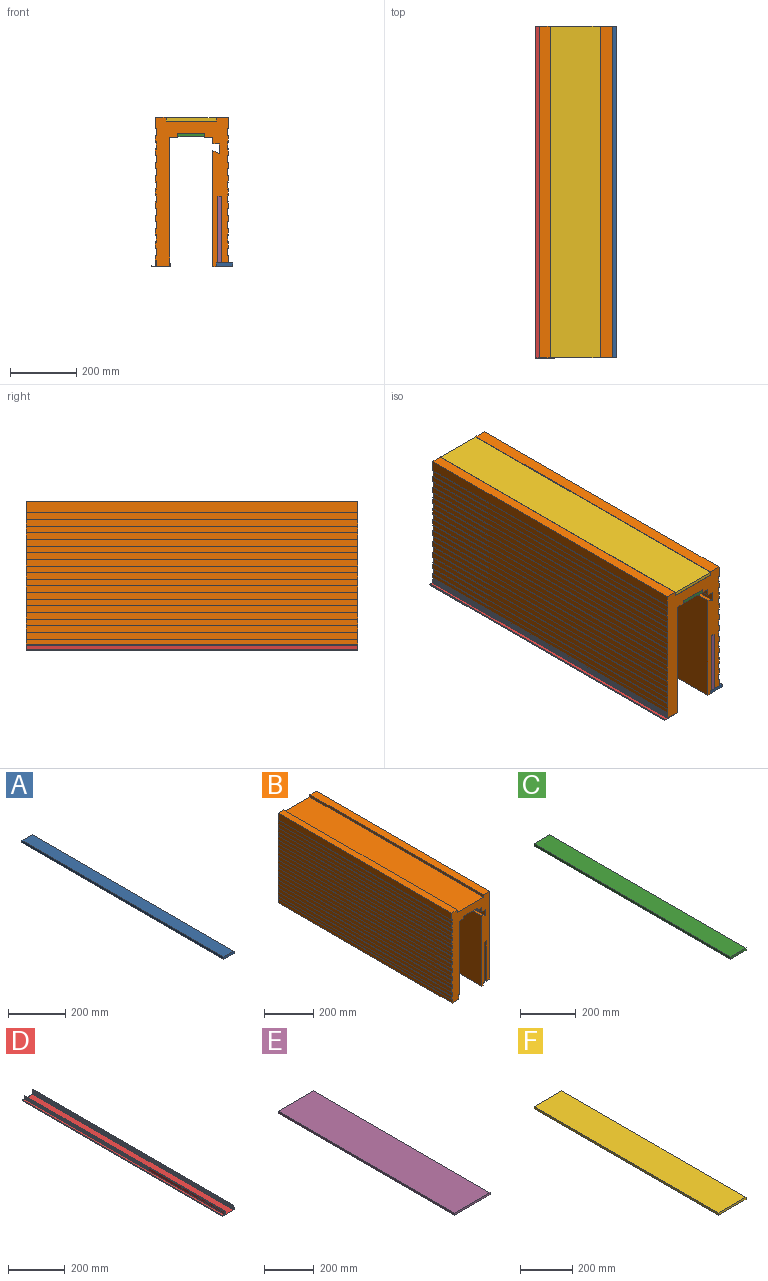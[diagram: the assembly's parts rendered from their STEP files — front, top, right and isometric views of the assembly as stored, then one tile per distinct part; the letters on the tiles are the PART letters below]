
ASSEMBLY  parts=6 mates=5
PART A: 6 faces, bbox 50x1000x10 mm
  f0: plane 1000x10mm, normal (-1,0,0), area 10000mm2, adj f1,f3,f4,f5
  f1: plane 1000x50mm, normal (0,0,-1), area 50000mm2, adj f0,f2,f4,f5
  f2: plane 1000x10mm, normal (1,0,0), area 10000mm2, adj f1,f3,f4,f5
  f3: plane 1000x50mm, normal (0,0,1), area 50000mm2, adj f0,f2,f4,f5
  f4: plane 50x10mm, normal (0,-1,0), area 500mm2, adj f0,f1,f2,f3
  f5: plane 50x10mm, normal (0,1,0), area 500mm2, adj f0,f1,f2,f3
PART B: 112 faces, bbox 220x1000x450 mm
  f0: plane 1000x35mm, normal (1,0,0), area 35000mm2, adj f1,f109,f110,f111
  f1: plane 1000x36.6mm, normal (0,0,1), area 36600mm2, adj f0,f2,f110,f111
  f2: plane 1000x11.5mm, normal (-1,0,0), area 11500mm2, adj f1,f3,f110,f111
  f3: plane 1000x151mm, normal (0,0,1), area 151000mm2, adj f2,f4,f110,f111
  f4: plane 1000x11.5mm, normal (1,0,0), area 11500mm2, adj f3,f5,f110,f111
  f5: plane 1000x32.4mm, normal (0,0,1), area 32400mm2, adj f4,f6,f110,f111
  f6: plane 1000x35mm, normal (-1,0,0), area 35000mm2, adj f5,f7,f110,f111
  f7: plane 1000x2mm, normal (0.45,0,-0.89), area 2236.1mm2, adj f6,f8,f110,f111
  f8: plane 1000x22mm, normal (-1,0,0), area 22000mm2, adj f7,f9,f110,f111
  f9: plane 1000x2mm, normal (0.45,0,0.89), area 2236.1mm2, adj f8,f10,f110,f111
  f10: plane 1000x20mm, normal (-1,0,0), area 20000mm2, adj f9,f11,f110,f111
  f11: plane 1000x2mm, normal (0.45,0,-0.89), area 2236.1mm2, adj f10,f12,f110,f111
  f12: plane 1000x22mm, normal (-1,0,0), area 22000mm2, adj f11,f13,f110,f111
  f13: plane 1000x2mm, normal (0.45,0,0.89), area 2236.1mm2, adj f12,f14,f110,f111
  f14: plane 1000x20mm, normal (-1,0,0), area 20000mm2, adj f13,f15,f110,f111
  f15: plane 1000x2mm, normal (0.45,0,-0.89), area 2236.1mm2, adj f14,f16,f110,f111
  f16: plane 1000x22mm, normal (-1,0,0), area 22000mm2, adj f15,f17,f110,f111
  f17: plane 1000x2mm, normal (0.45,0,0.89), area 2236.1mm2, adj f16,f18,f110,f111
  f18: plane 1000x20mm, normal (-1,0,0), area 20000mm2, adj f17,f19,f110,f111
  f19: plane 1000x2mm, normal (0.45,0,-0.89), area 2236.1mm2, adj f18,f20,f110,f111
  f20: plane 1000x22mm, normal (-1,0,0), area 22000mm2, adj f19,f21,f110,f111
  f21: plane 1000x2mm, normal (0.45,0,0.89), area 2236.1mm2, adj f20,f22,f110,f111
  f22: plane 1000x20mm, normal (-1,0,0), area 20000mm2, adj f21,f23,f110,f111
  f23: plane 1000x2mm, normal (0.45,0,-0.89), area 2236.1mm2, adj f22,f24,f110,f111
  f24: plane 1000x22mm, normal (-1,0,0), area 22000mm2, adj f23,f25,f110,f111
  f25: plane 1000x2mm, normal (0.45,0,0.89), area 2236.1mm2, adj f24,f26,f110,f111
  f26: plane 1000x20mm, normal (-1,0,0), area 20000mm2, adj f25,f27,f110,f111
  f27: plane 1000x2mm, normal (0.45,0,-0.89), area 2236.1mm2, adj f26,f28,f110,f111
  f28: plane 1000x22mm, normal (-1,0,0), area 22000mm2, adj f27,f29,f110,f111
  f29: plane 1000x2mm, normal (0.45,0,0.89), area 2236.1mm2, adj f28,f30,f110,f111
  f30: plane 1000x20mm, normal (-1,0,0), area 20000mm2, adj f29,f31,f110,f111
  f31: plane 1000x2mm, normal (0.45,0,-0.89), area 2236.1mm2, adj f30,f32,f110,f111
  f32: plane 1000x22mm, normal (-1,0,0), area 22000mm2, adj f31,f33,f110,f111
  f33: plane 1000x2mm, normal (0.45,0,0.89), area 2236.1mm2, adj f32,f34,f110,f111
  f34: plane 1000x20mm, normal (-1,0,0), area 20000mm2, adj f33,f35,f110,f111
  f35: plane 1000x2mm, normal (0.45,0,-0.89), area 2236.1mm2, adj f34,f36,f110,f111
  f36: plane 1000x22mm, normal (-1,0,0), area 22000mm2, adj f35,f37,f110,f111
  f37: plane 1000x2mm, normal (0.45,0,0.89), area 2236.1mm2, adj f36,f38,f110,f111
  f38: plane 1000x20mm, normal (-1,0,0), area 20000mm2, adj f37,f39,f110,f111
  f39: plane 1000x2mm, normal (0.45,0,-0.89), area 2236.1mm2, adj f38,f40,f110,f111
  f40: plane 1000x22mm, normal (-1,0,0), area 22000mm2, adj f39,f41,f110,f111
  f41: plane 1000x2mm, normal (0.45,0,0.89), area 2236.1mm2, adj f40,f42,f110,f111
  f42: plane 1000x20mm, normal (-1,0,0), area 20000mm2, adj f41,f43,f110,f111
  f43: plane 1000x2mm, normal (0.45,0,-0.89), area 2236.1mm2, adj f42,f44,f110,f111
  f44: plane 1000x22mm, normal (-1,0,0), area 22000mm2, adj f43,f45,f110,f111
  f45: plane 1000x2mm, normal (0.45,0,0.89), area 2236.1mm2, adj f44,f46,f110,f111
  f46: plane 1000x15mm, normal (-1,0,0), area 15000mm2, adj f45,f47,f110,f111
  f47: plane 1000x1.9mm, normal (0,0,-1), area 1899.3mm2, adj f46,f48,f110,f111
  f48: plane 1000x18.5mm, normal (-1,0,0), area 18504.2mm2, adj f47,f49,f110,f111
  f49: plane 1000x39.1mm, normal (0,0,-1), area 39100mm2, adj f48,f50,f110,f111
  f50: plane 1000x21.53mm, normal (1,0,0), area 21529.7mm2, adj f49,f51,f110,f111
  f51: plane 1000x1.9mm, normal (0,0,-1), area 1900.7mm2, adj f50,f52,f110,f111
  f52: plane 1000x367mm, normal (1,0,0), area 367000mm2, adj f51,f53,f110,f111
  f53: plane 1000x24.5mm, normal (0,0,-1), area 24500mm2, adj f52,f54,f110,f111
  f54: plane 1000x11.5mm, normal (1,0,0), area 11500mm2, adj f53,f55,f110,f111
  f55: plane 1000x81mm, normal (0,0,-1), area 81000mm2, adj f54,f56,f110,f111
  f56: plane 1000x11.5mm, normal (-1,0,0), area 11500mm2, adj f55,f57,f110,f111
  f57: plane 1000x24.5mm, normal (0,0,-1), area 24500mm2, adj f56,f58,f110,f111
  f58: plane 1000x20mm, normal (-1,0,0), area 20000mm2, adj f57,f59,f110,f111
  f59: plane 1000x20mm, normal (0,0,-1), area 20000mm2, adj f58,f60,f110,f111
  f60: plane 1000x30mm, normal (-1,0,0), area 30000mm2, adj f59,f61,f110,f111
  f61: plane 1000x20mm, normal (0.45,0,0.89), area 22360.7mm2, adj f60,f62,f110,f111
  f62: plane 1000x350mm, normal (-1,0,0), area 350000mm2, adj f61,f63,f110,f111
  f63: plane 1000x10.1mm, normal (0,0,-1), area 10100mm2, adj f62,f64,f110,f111
  f64: plane 1000x11.5mm, normal (1,0,0), area 11500mm2, adj f63,f65,f110,f111
  f65: plane 1000x5mm, normal (0,0,-1), area 5000mm2, adj f64,f66,f110,f111
  f66: plane 1000x201mm, normal (1,0,0), area 201000mm2, adj f65,f67,f110,f111
  f67: plane 1000x10.8mm, normal (0,0,-1), area 10800mm2, adj f66,f68,f110,f111
  f68: plane 1000x201mm, normal (-1,0,0), area 201000mm2, adj f67,f69,f110,f111
  f69: plane 1000x21.2mm, normal (0,0,-1), area 21200mm2, adj f68,f70,f110,f111
  f70: plane 1000x23.5mm, normal (1,0,0), area 23500mm2, adj f69,f71,f110,f111
  f71: plane 1000x2mm, normal (-0.45,0,0.89), area 2236.1mm2, adj f70,f72,f110,f111
  f72: plane 1000x22mm, normal (1,0,0), area 22000mm2, adj f71,f73,f110,f111
  f73: plane 1000x2mm, normal (-0.45,0,-0.89), area 2236.1mm2, adj f72,f74,f110,f111
  f74: plane 1000x20mm, normal (1,0,0), area 20000mm2, adj f73,f75,f110,f111
  f75: plane 1000x2mm, normal (-0.45,0,0.89), area 2236.1mm2, adj f74,f76,f110,f111
  f76: plane 1000x22mm, normal (1,0,0), area 22000mm2, adj f75,f77,f110,f111
  f77: plane 1000x2mm, normal (-0.45,0,-0.89), area 2236.1mm2, adj f76,f78,f110,f111
  f78: plane 1000x20mm, normal (1,0,0), area 20000mm2, adj f77,f79,f110,f111
  f79: plane 1000x2mm, normal (-0.45,0,0.89), area 2236.1mm2, adj f78,f80,f110,f111
  f80: plane 1000x22mm, normal (1,0,0), area 22000mm2, adj f79,f81,f110,f111
  f81: plane 1000x2mm, normal (-0.45,0,-0.89), area 2236.1mm2, adj f80,f82,f110,f111
  f82: plane 1000x20mm, normal (1,0,0), area 20000mm2, adj f81,f83,f110,f111
  f83: plane 1000x2mm, normal (-0.45,0,0.89), area 2236.1mm2, adj f82,f84,f110,f111
  f84: plane 1000x22mm, normal (1,0,0), area 22000mm2, adj f83,f85,f110,f111
  f85: plane 1000x2mm, normal (-0.45,0,-0.89), area 2236.1mm2, adj f84,f86,f110,f111
  f86: plane 1000x20mm, normal (1,0,0), area 20000mm2, adj f85,f87,f110,f111
  f87: plane 1000x2mm, normal (-0.45,0,0.89), area 2236.1mm2, adj f86,f88,f110,f111
  f88: plane 1000x22mm, normal (1,0,0), area 22000mm2, adj f87,f89,f110,f111
  f89: plane 1000x2mm, normal (-0.45,0,-0.89), area 2236.1mm2, adj f88,f90,f110,f111
  f90: plane 1000x20mm, normal (1,0,0), area 20000mm2, adj f89,f91,f110,f111
  f91: plane 1000x2mm, normal (-0.45,0,0.89), area 2236.1mm2, adj f90,f92,f110,f111
  f92: plane 1000x22mm, normal (1,0,0), area 22000mm2, adj f91,f93,f110,f111
  f93: plane 1000x2mm, normal (-0.45,0,-0.89), area 2236.1mm2, adj f92,f94,f110,f111
  f94: plane 1000x20mm, normal (1,0,0), area 20000mm2, adj f93,f95,f110,f111
  f95: plane 1000x2mm, normal (-0.45,0,0.89), area 2236.1mm2, adj f94,f96,f110,f111
  f96: plane 1000x22mm, normal (1,0,0), area 22000mm2, adj f95,f97,f110,f111
  f97: plane 1000x2mm, normal (-0.45,0,-0.89), area 2236.1mm2, adj f96,f98,f110,f111
  f98: plane 1000x20mm, normal (1,0,0), area 20000mm2, adj f97,f99,f110,f111
  f99: plane 1000x2mm, normal (-0.45,0,0.89), area 2236.1mm2, adj f98,f100,f110,f111
  f100: plane 1000x22mm, normal (1,0,0), area 22000mm2, adj f99,f101,f110,f111
  f101: plane 1000x2mm, normal (-0.45,0,-0.89), area 2236.1mm2, adj f100,f102,f110,f111
  f102: plane 1000x20mm, normal (1,0,0), area 20000mm2, adj f101,f103,f110,f111
  f103: plane 1000x2mm, normal (-0.45,0,0.89), area 2236.1mm2, adj f102,f104,f110,f111
  f104: plane 1000x22mm, normal (1,0,0), area 22000mm2, adj f103,f105,f110,f111
  f105: plane 1000x2mm, normal (-0.45,0,-0.89), area 2236.1mm2, adj f104,f106,f110,f111
  f106: plane 1000x20mm, normal (1,0,0), area 20000mm2, adj f105,f107,f110,f111
  f107: plane 1000x2mm, normal (-0.45,0,0.89), area 2236.1mm2, adj f106,f108,f110,f111
  f108: plane 1000x22mm, normal (1,0,0), area 22000mm2, adj f107,f109,f110,f111
  f109: plane 1000x2mm, normal (-0.45,0,-0.89), area 2236.1mm2, adj f0,f108,f110,f111
  f110: plane 450x220mm, normal (0,-1,0), area 41556mm2, adj f0,f1,f2,f3,f4,f5,f6,f7
  f111: plane 450x220mm, normal (0,1,0), area 41556mm2, adj f0,f1,f2,f3,f4,f5,f6,f7
PART C: 6 faces, bbox 80x1000x10 mm
  f0: plane 1000x10mm, normal (-1,0,0), area 10000mm2, adj f1,f3,f4,f5
  f1: plane 1000x80mm, normal (0,0,-1), area 80000mm2, adj f0,f2,f4,f5
  f2: plane 1000x10mm, normal (1,0,0), area 10000mm2, adj f1,f3,f4,f5
  f3: plane 1000x80mm, normal (0,0,1), area 80000mm2, adj f0,f2,f4,f5
  f4: plane 80x10mm, normal (0,-1,0), area 800mm2, adj f0,f1,f2,f3
  f5: plane 80x10mm, normal (0,1,0), area 800mm2, adj f0,f1,f2,f3
PART D: 62 faces, bbox 57.5x1000x21 mm
  f0: plane 1000x14.3mm, normal (-1,0,0), area 14303.9mm2, adj f1,f2,f60,f61
  f1: plane 57.5x21mm, normal (0,-1,0), area 145.8mm2, adj f0,f2,f3,f4,f5,f6,f7,f8
  f2: plane 1000x11mm, normal (0,0,1), area 11000mm2, adj f0,f1,f3,f60
  f3: plane 1000x1.5mm, normal (1,0,0), area 1500mm2, adj f1,f2,f4,f60
  f4: plane 1000x1.5mm, normal (0,0,1), area 1500mm2, adj f1,f3,f5,f60
  f5: plane 1000x3mm, normal (-1,0,0), area 3000mm2, adj f1,f4,f6,f60
  f6: plane 1000x57.5mm, normal (0,0,-1), area 57500mm2, adj f1,f5,f7,f60
  f7: plane 1000x4mm, normal (1,0,0), area 4000mm2, adj f1,f6,f8,f60
  f8: plane 1000x1mm, normal (0,0,1), area 1000mm2, adj f1,f7,f9,f60
  f9: plane 1000x3mm, normal (-1,0,0), area 3000mm2, adj f1,f8,f10,f60
  f10: plane 1000x1mm, normal (0,0,1), area 1000mm2, adj f1,f9,f11,f60
  f11: plane 1000x7mm, normal (1,0,0), area 7000mm2, adj f1,f10,f12,f60
  f12: plane 1000x1mm, normal (0,0,-1), area 1000mm2, adj f1,f11,f13,f60
  f13: plane 1000x3mm, normal (-1,0,0), area 3000mm2, adj f1,f12,f14,f60
  f14: plane 1000x1mm, normal (0,0,-1), area 1000mm2, adj f1,f13,f15,f60
  f15: plane 1000x4mm, normal (1,0,0), area 4000mm2, adj f1,f14,f16,f60
  f16: plane 1000x2mm, normal (0,0,1), area 2000mm2, adj f1,f15,f17,f60
  f17: plane 1000x12mm, normal (1,0,0), area 12000mm2, adj f1,f16,f18,f60
  f18: plane 1000x1mm, normal (0,0,1), area 1000mm2, adj f1,f17,f19,f60
  f19: plane 1000x1.73mm, normal (-0.87,0,0.5), area 2000mm2, adj f1,f18,f20,f60
  f20: plane 1000x1mm, normal (0,0,-1), area 1000mm2, adj f1,f19,f21,f60
  f21: plane 1000x1.73mm, normal (-0.87,0,0.5), area 2000mm2, adj f1,f20,f22,f60
  f22: plane 1000x1mm, normal (0,0,-1), area 1000mm2, adj f1,f21,f23,f60
  f23: plane 1000x1.73mm, normal (-0.87,0,0.5), area 2000mm2, adj f1,f22,f24,f60
  f24: plane 1000x1mm, normal (0,0,-1), area 1000mm2, adj f1,f23,f25,f60
  f25: plane 1000x1.73mm, normal (-0.87,0,0.5), area 2000mm2, adj f1,f24,f26,f60
  f26: plane 1000x1mm, normal (0,0,-1), area 1000mm2, adj f1,f25,f27,f60
  f27: plane 1000x1.73mm, normal (-0.87,0,0.5), area 2000mm2, adj f1,f26,f28,f60
  f28: plane 1000x1mm, normal (0,0,-1), area 1000mm2, adj f1,f27,f29,f60
  f29: plane 1000x1.73mm, normal (-0.87,0,0.5), area 2000mm2, adj f1,f28,f30,f60
  f30: plane 1000x1mm, normal (0,0,-1), area 1000mm2, adj f1,f29,f31,f60
  f31: plane 1000x1.73mm, normal (-0.87,0,0.5), area 2000mm2, adj f1,f30,f32,f60
  f32: plane 1000x1mm, normal (0,0,-1), area 1000mm2, adj f1,f31,f33,f60
  f33: plane 1000x1.73mm, normal (-0.87,0,0.5), area 2000mm2, adj f1,f32,f34,f60
  f34: plane 1000x1mm, normal (0,0,-1), area 1000mm2, adj f1,f33,f35,f60
  f35: plane 1000x1.73mm, normal (-0.87,0,0.5), area 2000mm2, adj f1,f34,f36,f60
  f36: plane 1000x1mm, normal (0,0,-1), area 1000mm2, adj f1,f35,f37,f60
  f37: plane 1000x1.73mm, normal (-0.87,0,0.5), area 2000mm2, adj f1,f36,f38,f60
  f38: plane 1000x1mm, normal (0,0,-1), area 1000mm2, adj f1,f37,f39,f60
  f39: plane 1000x1.73mm, normal (-0.87,0,0.5), area 2000mm2, adj f1,f38,f40,f60
  f40: plane 1000x1mm, normal (0,0,-1), area 1000mm2, adj f1,f39,f41,f60
  f41: plane 1000x0.45mm, normal (-1,0,0), area 447.4mm2, adj f1,f40,f42,f60
  f42: plane 1000x41mm, normal (0,0,1), area 41000mm2, adj f1,f41,f43,f60
  f43: plane 1000x0.45mm, normal (1,0,0), area 447.4mm2, adj f1,f42,f44,f60
  f44: plane 1000x1mm, normal (0,0,-1), area 1000mm2, adj f1,f43,f45,f60
  f45: plane 1000x1.73mm, normal (0.87,0,0.5), area 2000mm2, adj f1,f44,f46,f60
  f46: plane 1000x1mm, normal (0,0,-1), area 1000mm2, adj f1,f45,f47,f60
  f47: plane 1000x1.73mm, normal (0.87,0,0.5), area 2000mm2, adj f1,f46,f48,f60
  f48: plane 1000x1mm, normal (0,0,-1), area 1000mm2, adj f1,f47,f49,f60
  f49: plane 1000x1.73mm, normal (0.87,0,0.5), area 2000mm2, adj f1,f48,f50,f60
  f50: plane 1000x1mm, normal (0,0,-1), area 1000mm2, adj f1,f49,f51,f60
  f51: plane 1000x1.73mm, normal (0.87,0,0.5), area 2000mm2, adj f1,f50,f52,f60
  f52: plane 1000x1mm, normal (0,0,-1), area 1000mm2, adj f1,f51,f53,f60
  f53: plane 1000x1.73mm, normal (0.87,0,0.5), area 2000mm2, adj f1,f52,f54,f60
  f54: plane 1000x1mm, normal (0,0,-1), area 1000mm2, adj f1,f53,f55,f60
  f55: plane 1000x1.73mm, normal (0.87,0,0.5), area 2000mm2, adj f1,f54,f56,f60
  f56: plane 1000x1mm, normal (0,0,-1), area 1000mm2, adj f1,f55,f57,f60
  f57: plane 1000x1.73mm, normal (0.87,0,0.5), area 2000mm2, adj f1,f56,f58,f60
  f58: plane 1000x1mm, normal (0,0,-1), area 1000mm2, adj f1,f57,f59,f60
  f59: plane 1000x1.73mm, normal (0.87,0,0.5), area 2000mm2, adj f1,f58,f60,f61
  f60: plane 57.5x21mm, normal (0,1,0), area 145.8mm2, adj f0,f2,f3,f4,f5,f6,f7,f8
  f61: plane 1000x1mm, normal (0,0,1), area 1000mm2, adj f0,f1,f59,f60
PART E: 6 faces, bbox 200x1000x10 mm
  f0: plane 1000x10mm, normal (-1,0,0), area 10000mm2, adj f1,f3,f4,f5
  f1: plane 1000x200mm, normal (0,0,-1), area 200000mm2, adj f0,f2,f4,f5
  f2: plane 1000x10mm, normal (1,0,0), area 10000mm2, adj f1,f3,f4,f5
  f3: plane 1000x200mm, normal (0,0,1), area 200000mm2, adj f0,f2,f4,f5
  f4: plane 200x10mm, normal (0,-1,0), area 2000mm2, adj f0,f1,f2,f3
  f5: plane 200x10mm, normal (0,1,0), area 2000mm2, adj f0,f1,f2,f3
PART F: 6 faces, bbox 150x1000x10 mm
  f0: plane 1000x10mm, normal (-1,0,0), area 10000mm2, adj f1,f3,f4,f5
  f1: plane 1000x150mm, normal (0,0,-1), area 150000mm2, adj f0,f2,f4,f5
  f2: plane 1000x10mm, normal (1,0,0), area 10000mm2, adj f1,f3,f4,f5
  f3: plane 1000x150mm, normal (0,0,1), area 150000mm2, adj f0,f2,f4,f5
  f4: plane 150x10mm, normal (0,-1,0), area 1500mm2, adj f0,f1,f2,f3
  f5: plane 150x10mm, normal (0,1,0), area 1500mm2, adj f0,f1,f2,f3
PLACE A t=(-424.39,353.04,-38.56)mm
PLACE B t=(-467.39,353.04,-259.56)mm
PLACE C t=(-539.49,353.04,351.44)mm
PLACE D t=(-562.49,353.04,-39.56)mm
PLACE E rot(axis=(0,1,0),90deg) t=(-418.89,353.04,172.44)mm
PLACE F t=(-574.49,353.04,399.44)mm
MATE fastened E.f4 <-> B.f110  axis (0,-1,0) through (-419.39,-646.96,172.94)mm
MATE fastened C.f4 <-> B.f110  axis (0,-1,0) through (-539.99,-646.96,361.94)mm
MATE fastened F.f4 <-> B.f110  axis (0,-1,0) through (-574.99,-646.96,398.94)mm
MATE fastened D.f1 <-> B.f110  axis (0,-1,0) through (-605.49,-646.96,-38.06)mm
MATE fastened A.f4 <-> B.f110  axis (0,-1,0) through (-424.39,-646.96,-28.06)mm
